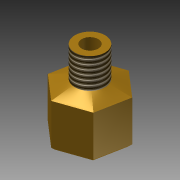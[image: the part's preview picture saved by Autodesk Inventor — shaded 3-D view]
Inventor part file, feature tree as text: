
AUTODESK INVENTOR PART (.ipt)
format: ipt  version: 2011 (Build 150239000, 239)  size: 131,072 bytes
history: native  units: mm (DEFAULTED — no unit token found)
features: sketch x5, extrude x4, thread x2, plane x1, loft x1, chamfer x1, projected_geometry x1
ambient origin geometry x8: Origin, YZ Plane, XZ Plane, XY Plane, X Axis, Y Axis, Z Axis, Center Point
bodies: Solid1 (feature_tree)
feature tree (15):
  extrude  "Extrusion1"  Depth=14.478mm TaperAngle=0.0deg
  plane  "Work Plane1"
  sketch  "Sketch2"  dims[d3=2.032mm d4=10.0mm]
  loft  "Loft1"
  extrude  "Extrusion2"  TaperAngle=0.0deg  [1 undecoded]
  extrude  "Extrusion3"  Depth=11.5mm
  extrude  "Extrusion4"  Depth=5.5mm
  thread  "Thread1"  [1 undecoded]
  thread  "Thread2"  [1 undecoded]
  chamfer  "Chamfer1"  [1 undecoded]
  sketch  "Sketch1"  dims[d0=19.05mm d1=14.478mm d2=0.0mm]
  sketch  "Sketch3"  dims[d5=0.0mm d6=90.0deg d7=0.0mm d8=90.0deg]
  projected_geometry  "Projected Loop1"
  sketch  "Sketch4"  dims[d9=10.0mm d10=0.0mm d11=11.5mm]
  sketch  "Sketch5"  dims[d12=11.75mm d13=0.0mm d14=5.5mm d15=19.0mm d16=0.0mm d17=10.0mm d18=0.0mm d19=10.0mm d20=0.0mm d21=1.0mm d22=2.0mm d23=45.0deg]
note: 4 required parameter values undecoded (feature->parameter linkage not recoverable at this tier; creation-order binding heuristic only, values carry confidence <= 0.55)
